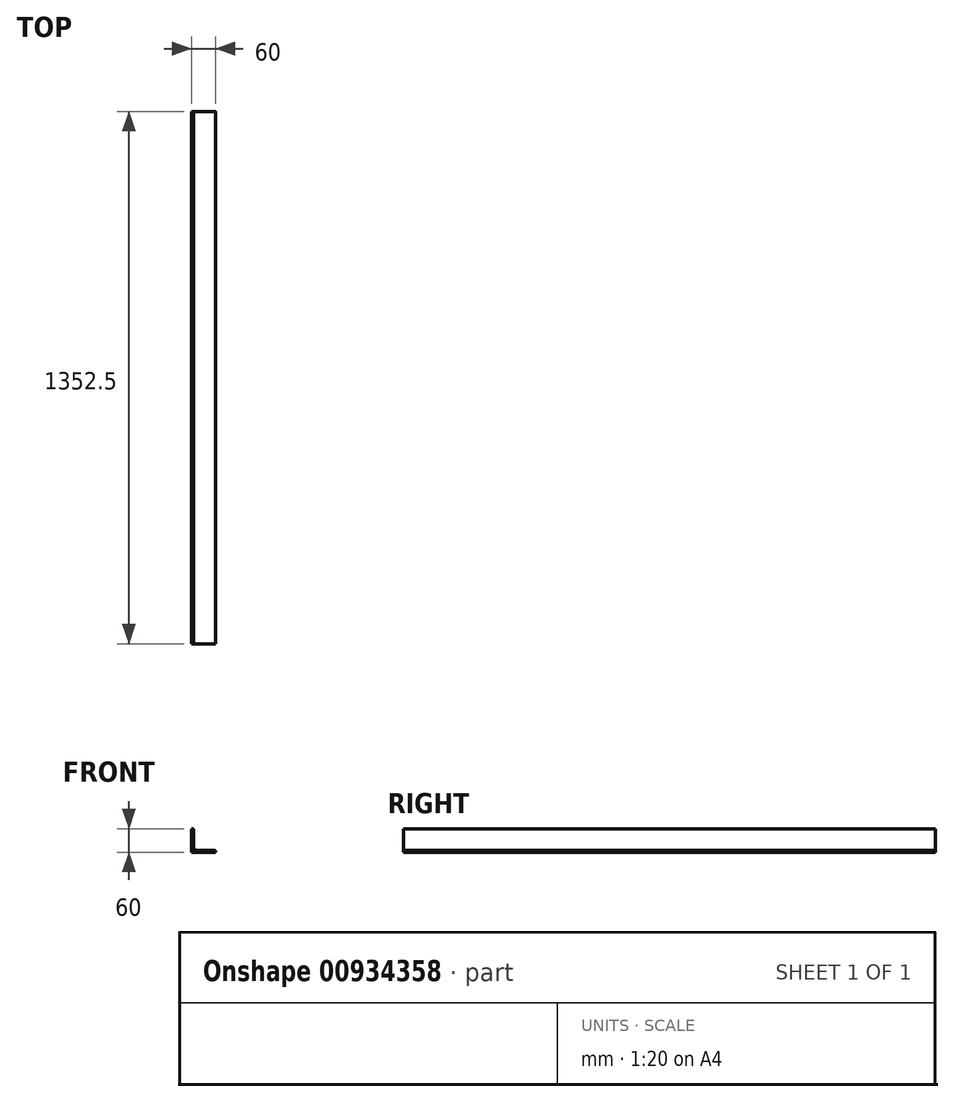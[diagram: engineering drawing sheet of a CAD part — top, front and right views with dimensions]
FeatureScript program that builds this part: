
annotation { "Feature Type Name" : "Feature", "Feature Type Description" : "" }
export const myFeature = defineFeature(function(context is Context, id is Id, definition is map)
    precondition{}
    {
        {
            var Q0;
            Q0=qCreatedBy(makeId("Front.planeOp"),FACE);
            var sketch = newSketch(context, id + "F0", { "sketchPlane" : qUnion([Q0])});
            skLineSegment(sketch, "E0", {"start": v(0, 0) * mm, "end": v(0, 60) * mm});
            skLineSegment(sketch, "E1", {"start": v(0, 0) * mm, "end": v(60, 0) * mm});
            skLineSegment(sketch, "E2.0", {"start": v(5, 13) * mm, "end": v(5, 57.6) * mm});
            skLineSegment(sketch, "E2.1", {"start": v(13, 5) * mm, "end": v(57.6, 5) * mm});
            skLineSegment(sketch, "E3", {"start": v(60, 0) * mm, "end": v(60, 2.6) * mm});
            skLineSegment(sketch, "E4", {"start": v(0, 60) * mm, "end": v(2.6, 60) * mm});
            skPoint(sketch, "E5.visualSharp", {"position": v(5, 60) * mm});
            skArc(sketch, "E5.filletArc", {"start": v(5, 57.6) * mm, "mid": v(4.3, 59.3) * mm, "end": v(2.6, 60) * mm});
            skPoint(sketch, "E6.visualSharp", {"position": v(60, 5) * mm});
            skArc(sketch, "E6.filletArc", {"start": v(60, 2.6) * mm, "mid": v(59.3, 4.3) * mm, "end": v(57.6, 5) * mm});
            skPoint(sketch, "E7.visualSharp", {"position": v(5, 5) * mm});
            skArc(sketch, "E7.filletArc", {"start": v(5, 13) * mm, "mid": v(7.34, 7.34) * mm, "end": v(13, 5) * mm});
            skSolve(sketch);
        }
        {
            var Q0;
            Q0=makeQuery(id+"F0.imprint","IMPRINT",FACE,{"disambiguationData":[TD([[makeQuery(id+"F0.imprint","IMPRINT",EDGE,{"derivedFrom":sQuery(id+"F0.wireOp",EDGE,"E0")}),-1.0]])]});
            extrude(context, id + "F1", {"entities" : qUnion([Q0]), "depth" : 1352.5 * mm, "offsetDistance" : 25 * mm});
        }
    });
